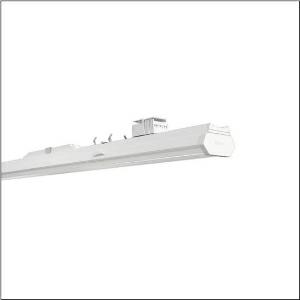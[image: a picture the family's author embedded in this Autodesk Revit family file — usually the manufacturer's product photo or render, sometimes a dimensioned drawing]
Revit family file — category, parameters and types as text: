
# Revit family: licross_r__11_protected_mo_51ts12dn58xf_38fb
name_source: partatom
category: Lighting Fixtures
units: mm (PartAtom-declared; Revit-internal decimal feet)

## family parameters
Cut with Voids When Loaded = No
Host = Face
Light Source = No
Part Type = Normal
Room Calculation Point = No
Round Connector Dimension = Use Diameter
Shared = No

## types (1)
- --- (1 x LED, 8480 lm, 56.2 W, 5000K)
    Apparent Load = 56 VA
    CIE Flux Codes = 54 82 95 97 100
    Color Rendering = 80
    Color Temperature = 5000K
    Default Elevation = 1800 mm
    Description = Licross® 11 Protected MOluminaire insert, length: 1.500mm, width: 90mm, height: 101mm, LED rated luminous flux: 8.480lm, light colour: 850, control gear: DALI 2, control gear: ECG DALI, with plug, 5-pole, with phase selection, mains connection: 220..240V, AC, 50/60Hz, halogen-free wiring, primary optical cover: cover, of PMMA, light emission: direct with ceiling illumination distribution, protection rating (complete): IP50, insulation class (complete): insulation class I (protective earthing), certification: CE, ENEC, VDE, protection symbol: D if used in an environment with non-conductive dust loads with corresponding accessories, permissible ambient temperature for indoor applications: -25..+40°C, reducing of maximum allowable ambient temperature of 5°C with ceiling mounting, corresponds to IFS (International Featured Standards) requirements for safety and quality in the food industry, packaging unit: 1 piece
    Height = 92 mm
    Lamp = 1 x LED
    Lamp Light Flux = 8480 lm
    Lamp Power = 56.2 W
    Lamp count = 1
    Length = 1500 mm
    Luminous efficacy = 151 lm/W
    Manufacturer = Siteco
    ModVariant = No
    Model = 51TS12DN58XF
    Mounting Place = Ceiling
    Mounting Type = Pendant
    Number of Poles = 1
    OnlyDefault = Yes
    Power Factor = 1
    Product Name = Licross® 11 Protected MO
    Product group = luminaire insert
    ProductGroupID = 902
    Protection Class = Protection class I
    Protection Degree = IP 50
    RLX_Detail_Level = 1
    RlxData = <blob elided: 23877 chars, md5=847c9936>
    Socket = socket
    Standby Power = 0 W
    System Light Flux = 8480 lm
    System Power = 56 W
    Type Comments = factory setting: luminous flux: 100 % | dim-lin: 254 | 370 mA
    Type Image = l_1256145.jpg
    URL = http://relux.com
    VarID = @adj_138105
    Voltage = 0 V
    Weight = 0.00 kg
    Width = 88 mm

## geometry (parser evidence)
native form markers: Blend x4, Sweep x11
no freeform markers — native parametric forms only
